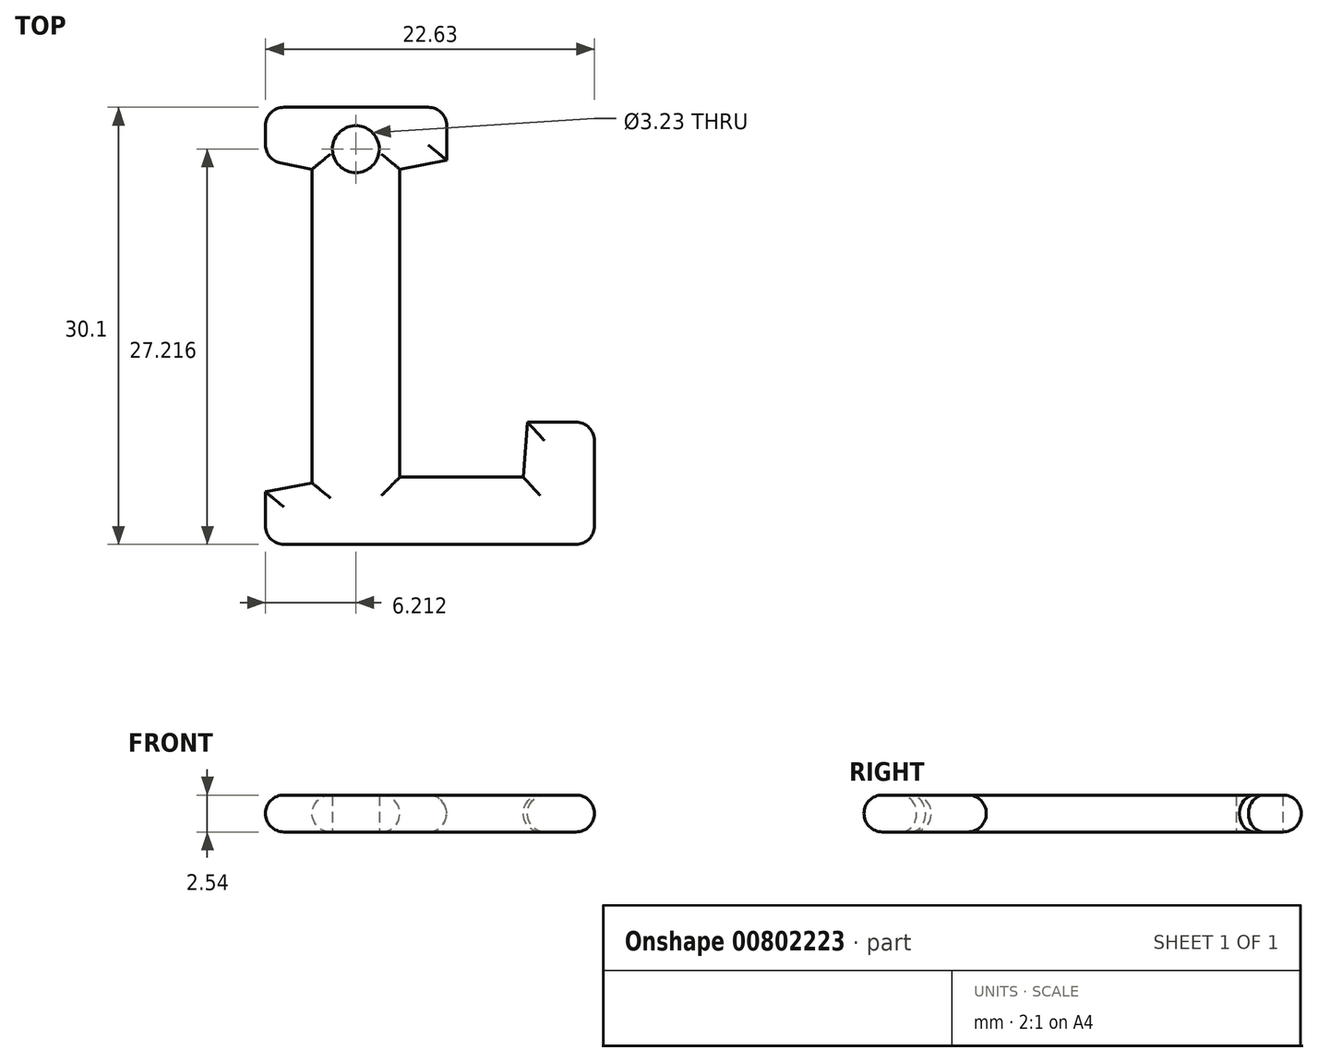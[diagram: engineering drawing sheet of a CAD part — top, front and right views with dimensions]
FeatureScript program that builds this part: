
annotation { "Feature Type Name" : "Feature", "Feature Type Description" : "" }
export const myFeature = defineFeature(function(context is Context, id is Id, definition is map)
    precondition{}
    {
        {
            var Q0;
            Q0=qCreatedBy(makeId("Top.planeOp"),FACE);
            var sketch = newSketch(context, id + "F0", { "sketchPlane" : qUnion([Q0])});
            skText(sketch, "E0", { "text": "L", "fontName": "RobotoSlab-Bold.ttf"});
            skCircle(sketch, "E1", {"center": v(2.8, 5.77) * mm, "radius": 1.61 * mm});
            const initialGuessF0  = {"E0": [-0.00457, -0.02145, 1, 0, 0.03048]};
            skSetInitialGuess(sketch, initialGuessF0);
            skSolve(sketch);
        }
        {
            var Q0;
            Q0 = qSketchRegion(id + "F0", true);
            extrude(context, id + "F1", {"entities" : qUnion([Q0]), "depth" : 2.54 * mm, "offsetDistance" : 25.4 * mm});
        }
        {
            var Q0;
            Q0=makeQuery(id+"F1.opExtrude","CAP_EDGE",EDGE,{"disambiguationData":[OSD([sQuery(id+"F0.wireOp",EDGE,"E0.sketch_text.stroke-2")])],"isStart":false});
            var Q1;
            Q1=makeQuery(id+"F1.opExtrude","CAP_EDGE",EDGE,{"disambiguationData":[OSD([sQuery(id+"F0.wireOp",EDGE,"E0.sketch_text.stroke-4")])],"isStart":false});
            var Q2;
            Q2=makeQuery(id+"F1.opExtrude","CAP_EDGE",EDGE,{"disambiguationData":[OSD([sQuery(id+"F0.wireOp",EDGE,"E0.sketch_text.stroke-10")])],"isStart":true});
            var Q3;
            Q3=makeQuery(id+"F1.opExtrude","CAP_EDGE",EDGE,{"disambiguationData":[OSD([sQuery(id+"F0.wireOp",EDGE,"E0.sketch_text.stroke-9")])],"isStart":true});
            var Q4;
            Q4=makeQuery(id+"F1.opExtrude","CAP_EDGE",EDGE,{"disambiguationData":[OSD([sQuery(id+"F0.wireOp",EDGE,"E0.sketch_text.stroke-3")])],"isStart":false});
            var Q5;
            Q5=makeQuery(id+"F1.opExtrude","CAP_EDGE",EDGE,{"disambiguationData":[OSD([sQuery(id+"F0.wireOp",EDGE,"E0.sketch_text.stroke-11")])],"isStart":false});
            var Q6;
            Q6=makeQuery(id+"F1.opExtrude","CAP_EDGE",EDGE,{"disambiguationData":[OSD([sQuery(id+"F0.wireOp",EDGE,"E0.sketch_text.stroke-12")])],"isStart":false});
            var Q7;
            Q7=makeQuery(id+"F1.opExtrude","CAP_EDGE",EDGE,{"disambiguationData":[OSD([sQuery(id+"F0.wireOp",EDGE,"E0.sketch_text.stroke-15")])],"isStart":false});
            var Q8;
            Q8=makeQuery(id+"F1.opExtrude","CAP_EDGE",EDGE,{"disambiguationData":[OSD([sQuery(id+"F0.wireOp",EDGE,"E0.sketch_text.stroke-0")])],"isStart":false});
            var Q9;
            Q9=makeQuery(id+"F1.opExtrude","CAP_EDGE",EDGE,{"disambiguationData":[OSD([sQuery(id+"F0.wireOp",EDGE,"E0.sketch_text.stroke-13")])],"isStart":false});
            var Q10;
            Q10=makeQuery(id+"F1.opExtrude","CAP_EDGE",EDGE,{"disambiguationData":[OSD([sQuery(id+"F0.wireOp",EDGE,"E0.sketch_text.stroke-1")])],"isStart":false});
            var Q11;
            Q11=makeQuery(id+"F1.opExtrude","CAP_EDGE",EDGE,{"disambiguationData":[OSD([sQuery(id+"F0.wireOp",EDGE,"E0.sketch_text.stroke-5"),sQuery(id+"F0.wireOp",EDGE,"E0.sketch_text.stroke-6"),sQuery(id+"F0.wireOp",EDGE,"E0.sketch_text.stroke-7")])],"isStart":false});
            var Q12;
            Q12=makeQuery(id+"F1.opExtrude","CAP_EDGE",EDGE,{"disambiguationData":[OSD([sQuery(id+"F0.wireOp",EDGE,"E0.sketch_text.stroke-14")])],"isStart":false});
            var Q13;
            Q13=makeQuery(id+"F1.opExtrude","CAP_EDGE",EDGE,{"disambiguationData":[OSD([sQuery(id+"F0.wireOp",EDGE,"E0.sketch_text.stroke-10")])],"isStart":false});
            var Q14;
            Q14=makeQuery(id+"F1.opExtrude","CAP_EDGE",EDGE,{"disambiguationData":[OSD([sQuery(id+"F0.wireOp",EDGE,"E0.sketch_text.stroke-9")])],"isStart":false});
            var Q15;
            Q15=makeQuery(id+"F1.opExtrude","CAP_EDGE",EDGE,{"disambiguationData":[OSD([sQuery(id+"F0.wireOp",EDGE,"E0.sketch_text.stroke-14")])],"isStart":true});
            var Q16;
            Q16=makeQuery(id+"F1.opExtrude","CAP_EDGE",EDGE,{"disambiguationData":[OSD([sQuery(id+"F0.wireOp",EDGE,"E0.sketch_text.stroke-13")])],"isStart":true});
            var Q17;
            Q17=makeQuery(id+"F1.opExtrude","CAP_EDGE",EDGE,{"disambiguationData":[OSD([sQuery(id+"F0.wireOp",EDGE,"E0.sketch_text.stroke-5"),sQuery(id+"F0.wireOp",EDGE,"E0.sketch_text.stroke-6"),sQuery(id+"F0.wireOp",EDGE,"E0.sketch_text.stroke-7")])],"isStart":true});
            var Q18;
            Q18=makeQuery(id+"F1.opExtrude","CAP_EDGE",EDGE,{"disambiguationData":[OSD([sQuery(id+"F0.wireOp",EDGE,"E0.sketch_text.stroke-2")])],"isStart":true});
            var Q19;
            Q19=makeQuery(id+"F1.opExtrude","CAP_EDGE",EDGE,{"disambiguationData":[OSD([sQuery(id+"F0.wireOp",EDGE,"E0.sketch_text.stroke-1")])],"isStart":true});
            var Q20;
            Q20=makeQuery(id+"F1.opExtrude","CAP_EDGE",EDGE,{"disambiguationData":[OSD([sQuery(id+"F0.wireOp",EDGE,"E0.sketch_text.stroke-0")])],"isStart":true});
            var Q21;
            Q21=makeQuery(id+"F1.opExtrude","SWEPT_EDGE",EDGE,{"disambiguationData":[OSD([sQuery(id+"F0.wireOp",EDGE,"E0.sketch_text.stroke-0"),sQuery(id+"F0.wireOp",EDGE,"E0.sketch_text.stroke-15")])]});
            var Q22;
            Q22=makeQuery(id+"F1.opExtrude","CAP_EDGE",EDGE,{"disambiguationData":[OSD([sQuery(id+"F0.wireOp",EDGE,"E0.sketch_text.stroke-4")])],"isStart":true});
            var Q23;
            Q23=makeQuery(id+"F1.opExtrude","CAP_EDGE",EDGE,{"disambiguationData":[OSD([sQuery(id+"F0.wireOp",EDGE,"E0.sketch_text.stroke-8")])],"isStart":true});
            var Q24;
            Q24=makeQuery(id+"F1.opExtrude","SWEPT_EDGE",EDGE,{"disambiguationData":[OSD([sQuery(id+"F0.wireOp",EDGE,"E0.sketch_text.stroke-14"),sQuery(id+"F0.wireOp",EDGE,"E0.sketch_text.stroke-15")])]});
            var Q25;
            Q25=makeQuery(id+"F1.opExtrude","SWEPT_EDGE",EDGE,{"disambiguationData":[OSD([sQuery(id+"F0.wireOp",EDGE,"E0.sketch_text.stroke-7"),sQuery(id+"F0.wireOp",EDGE,"E0.sketch_text.stroke-8")])]});
            var Q26;
            Q26=makeQuery(id+"F1.opExtrude","CAP_EDGE",EDGE,{"disambiguationData":[OSD([sQuery(id+"F0.wireOp",EDGE,"E0.sketch_text.stroke-11")])],"isStart":true});
            var Q27;
            Q27=makeQuery(id+"F1.opExtrude","CAP_EDGE",EDGE,{"disambiguationData":[OSD([sQuery(id+"F0.wireOp",EDGE,"E0.sketch_text.stroke-12")])],"isStart":true});
            var Q28;
            Q28=makeQuery(id+"F1.opExtrude","CAP_EDGE",EDGE,{"disambiguationData":[OSD([sQuery(id+"F0.wireOp",EDGE,"E0.sketch_text.stroke-3")])],"isStart":true});
            var Q29;
            Q29=makeQuery(id+"F1.opExtrude","CAP_EDGE",EDGE,{"disambiguationData":[OSD([sQuery(id+"F0.wireOp",EDGE,"E0.sketch_text.stroke-8")])],"isStart":false});
            var Q30;
            Q30=makeQuery(id+"F1.opExtrude","SWEPT_EDGE",EDGE,{"disambiguationData":[OSD([sQuery(id+"F0.wireOp",EDGE,"E0.sketch_text.stroke-13"),sQuery(id+"F0.wireOp",EDGE,"E0.sketch_text.stroke-14")])]});
            var Q31;
            Q31=makeQuery(id+"F1.opExtrude","CAP_EDGE",EDGE,{"disambiguationData":[OSD([sQuery(id+"F0.wireOp",EDGE,"E0.sketch_text.stroke-15")])],"isStart":true});
            var Q32;
            Q32=makeQuery(id+"F1.opExtrude","SWEPT_EDGE",EDGE,{"disambiguationData":[OSD([sQuery(id+"F0.wireOp",EDGE,"E0.sketch_text.stroke-3"),sQuery(id+"F0.wireOp",EDGE,"E0.sketch_text.stroke-4")])]});
            var Q33;
            Q33=makeQuery(id+"F1.opExtrude","SWEPT_EDGE",EDGE,{"disambiguationData":[OSD([sQuery(id+"F0.wireOp",EDGE,"E0.sketch_text.stroke-4"),sQuery(id+"F0.wireOp",EDGE,"E0.sketch_text.stroke-5")])]});
            fillet(context, id + "F2", {"entities" : qUnion([Q0, Q1, Q2, Q3, Q4, Q5, Q6, Q7, Q8, Q9, Q10, Q11, Q12, Q13, Q14, Q15, Q16, Q17, Q18, Q19, Q20, Q21, Q22, Q23, Q24, Q25, Q26, Q27, Q28, Q29, Q30, Q31, Q32, Q33]), "radius" : 1.27 * mm, "allowEdgeOverflow" : false});
        }
    });
